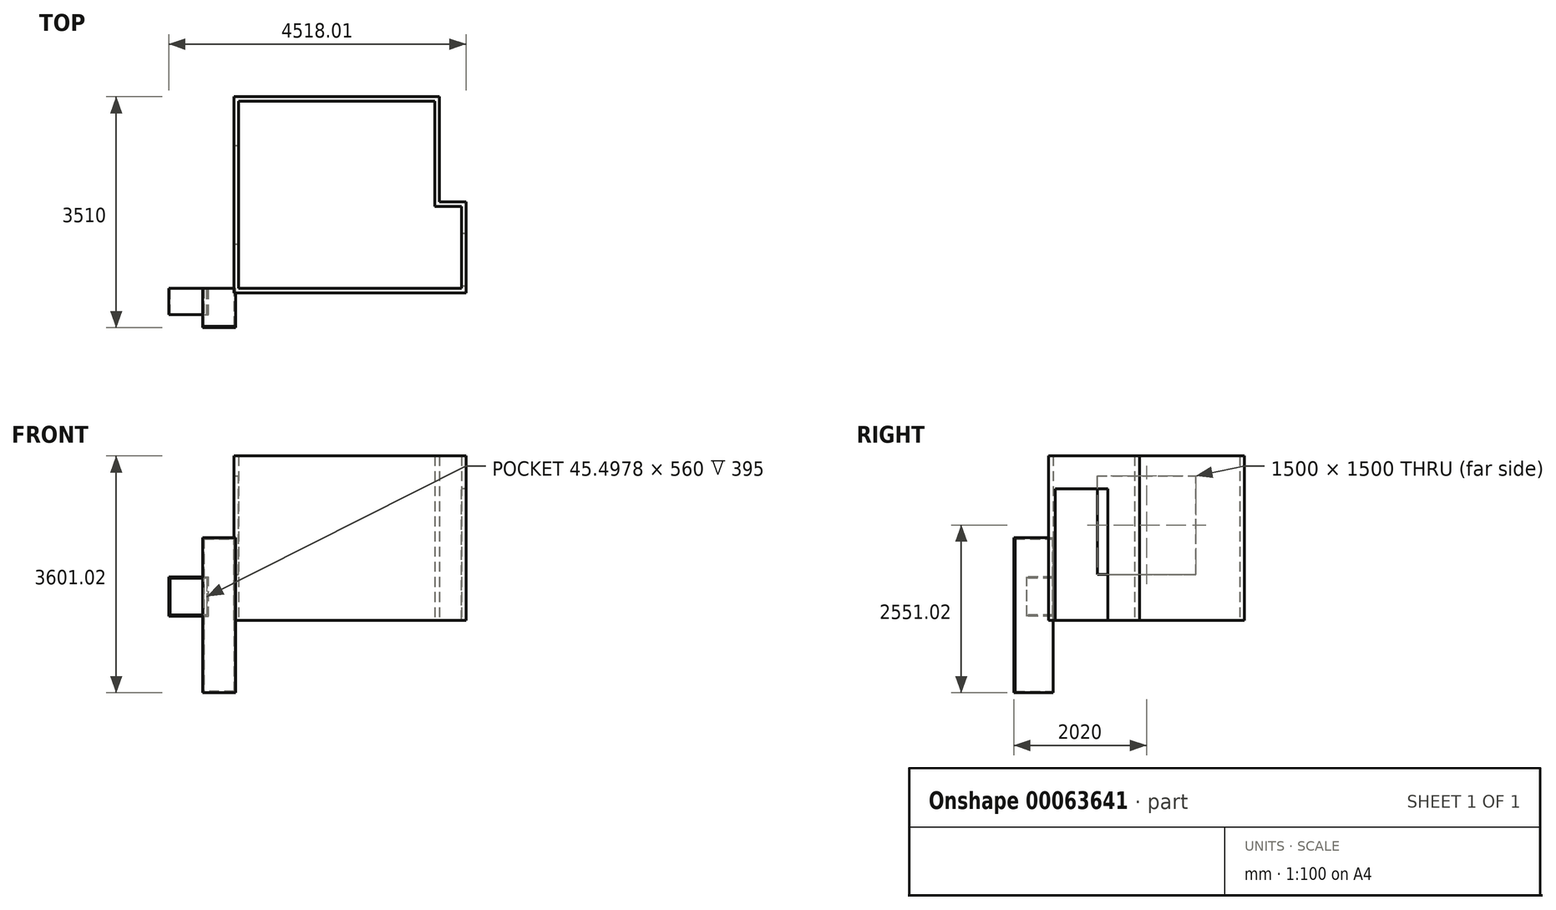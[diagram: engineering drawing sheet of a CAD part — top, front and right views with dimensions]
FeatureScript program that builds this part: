
annotation { "Feature Type Name" : "Feature", "Feature Type Description" : "" }
export const myFeature = defineFeature(function(context is Context, id is Id, definition is map)
    precondition{}
    {
        {
            var Q0;
            Q0=qCreatedBy(makeId("Top.planeOp"),FACE);
            var sketch = newSketch(context, id + "F0", { "sketchPlane" : qUnion([Q0])});
            skLineSegment(sketch, "E0.bottom", {"start": v(0, 0) * mm, "end": v(3390, 0) * mm});
            skLineSegment(sketch, "E0.top", {"start": v(0, 2840) * mm, "end": v(2985, 2840) * mm});
            skLineSegment(sketch, "E0.left", {"start": v(0, 0) * mm, "end": v(0, 2840) * mm});
            skLineSegment(sketch, "E0.right", {"start": v(2985, 1240) * mm, "end": v(2985, 2840) * mm});
            skLineSegment(sketch, "E1", {"start": v(3390, 0) * mm, "end": v(3390, 830) * mm});
            skLineSegment(sketch, "E2", {"start": v(3390, 830) * mm, "end": v(3390, 1240) * mm});
            skLineSegment(sketch, "E3", {"start": v(3390, 1240) * mm, "end": v(2985, 1240) * mm});
            skLineSegment(sketch, "E4.0", {"start": v(3460, 830) * mm, "end": v(3460, 1310) * mm});
            skLineSegment(sketch, "E4.1", {"start": v(3460, -70) * mm, "end": v(3460, 830) * mm});
            skLineSegment(sketch, "E4.2", {"start": v(3055, 1310) * mm, "end": v(3055, 2910) * mm});
            skLineSegment(sketch, "E4.3", {"start": v(-70, 2910) * mm, "end": v(3055, 2910) * mm});
            skLineSegment(sketch, "E4.4", {"start": v(-70, -70) * mm, "end": v(-70, 2910) * mm});
            skLineSegment(sketch, "E4.5", {"start": v(3460, 1310) * mm, "end": v(3055, 1310) * mm});
            skLineSegment(sketch, "E4.6", {"start": v(-70, -70) * mm, "end": v(3460, -70) * mm});
            skSolve(sketch);
        }
        {
            var Q0;
            Q0 = qSketchRegion(id + "F0", true);
            extrude(context, id + "F1", {"entities" : qUnion([Q0]), "depth" : 2500 * mm});
        }
        {
            var Q0;
            Q0=makeQuery(id+"F1.opExtrude","SWEPT_FACE",FACE,{"disambiguationData":[OSD([sQuery(id+"F0.wireOp",EDGE,"E1"),sQuery(id+"F0.wireOp",EDGE,"E2")])]});
            var sketch = newSketch(context, id + "F2", { "sketchPlane" : qUnion([Q0])});
            skLineSegment(sketch, "E5.0", {"start": v(0, 2500) * mm, "end": v(0, 0) * mm, "construction": true});
            skLineSegment(sketch, "E6.bottom", {"start": v(-830, 0) * mm, "end": v(-30, 0) * mm});
            skLineSegment(sketch, "E6.top", {"start": v(-830, 2000) * mm, "end": v(-30, 2000) * mm});
            skLineSegment(sketch, "E6.left", {"start": v(-830, 0) * mm, "end": v(-830, 2000) * mm});
            skLineSegment(sketch, "E6.right", {"start": v(-30, 0) * mm, "end": v(-30, 2000) * mm});
            skSolve(sketch);
        }
        {
            var Q0;
            Q0 = qSketchRegion(id + "F2", true);
            extrude(context, id + "F3", {"entities" : qUnion([Q0]), "operationType" : NewBodyOperationType.REMOVE, "endBound" : BoundingType.UP_TO_NEXT, "oppositeDirection" : true, "depth" : 25 * mm});
        }
        {
            var Q0;
            Q0=makeQuery(id+"F1.opExtrude","SWEPT_FACE",FACE,{"disambiguationData":[OSD([sQuery(id+"F0.wireOp",EDGE,"E0.left")])]});
            var sketch = newSketch(context, id + "F4", { "sketchPlane" : qUnion([Q0])});
            skLineSegment(sketch, "E7.bottom", {"start": v(670, 700) * mm, "end": v(2170, 700) * mm});
            skLineSegment(sketch, "E7.top", {"start": v(670, 2200) * mm, "end": v(2170, 2200) * mm});
            skLineSegment(sketch, "E7.left", {"start": v(670, 700) * mm, "end": v(670, 2200) * mm});
            skLineSegment(sketch, "E7.right", {"start": v(2170, 700) * mm, "end": v(2170, 2200) * mm});
            skSolve(sketch);
        }
        {
            var Q0;
            Q0 = qSketchRegion(id + "F4", true);
            extrude(context, id + "F5", {"entities" : qUnion([Q0]), "operationType" : NewBodyOperationType.REMOVE, "endBound" : BoundingType.UP_TO_NEXT, "oppositeDirection" : true, "depth" : 25 * mm});
        }
        {
            var Q0;
            Q0=qCreatedBy(makeId("Front.planeOp"),FACE);
            var sketch = newSketch(context, id + "F6", { "sketchPlane" : qUnion([Q0])});
            skLineSegment(sketch, "E8.bottom", {"start": v(-543.5, 1258.98) * mm, "end": v(-43.5, 1258.98) * mm});
            skLineSegment(sketch, "E8.top", {"start": v(-543.5, -1101.02) * mm, "end": v(-43.5, -1101.02) * mm});
            skLineSegment(sketch, "E8.left", {"start": v(-543.5, 1258.98) * mm, "end": v(-543.5, -1101.02) * mm});
            skLineSegment(sketch, "E8.right", {"start": v(-43.5, 1258.98) * mm, "end": v(-43.5, -1101.02) * mm});
            skLineSegment(sketch, "E9.0", {"start": v(-523.5, 1238.98) * mm, "end": v(-63.5, 1238.98) * mm});
            skLineSegment(sketch, "E9.1", {"start": v(-523.5, 1238.98) * mm, "end": v(-523.5, -1081.02) * mm});
            skLineSegment(sketch, "E9.2", {"start": v(-523.5, -1081.02) * mm, "end": v(-63.5, -1081.02) * mm});
            skLineSegment(sketch, "E9.3", {"start": v(-63.5, 1238.98) * mm, "end": v(-63.5, -1081.02) * mm});
            skSolve(sketch);
        }
        {
            var Q0;
            Q0 = qSketchRegion(id + "F6", true);
            extrude(context, id + "F7", {"entities" : qUnion([Q0]), "depth" : 580 * mm});
        }
        {
            var Q0;
            Q0=makeQuery(id+"F7.opExtrude","CAP_FACE",FACE,{"disambiguationData":[OSD([sQuery(id+"F6.wireOp",EDGE,"E8.bottom"),sQuery(id+"F6.wireOp",EDGE,"E8.top"),sQuery(id+"F6.wireOp",EDGE,"E8.left"),sQuery(id+"F6.wireOp",EDGE,"E8.right"),sQuery(id+"F6.wireOp",EDGE,"E9.0"),sQuery(id+"F6.wireOp",EDGE,"E9.1"),sQuery(id+"F6.wireOp",EDGE,"E9.2"),sQuery(id+"F6.wireOp",EDGE,"E9.3")])],"isStart":true});
            var sketch = newSketch(context, id + "F8", { "sketchPlane" : qUnion([Q0])});
            skLineSegment(sketch, "E10.bottom", {"start": v(43.5, -1101.02) * mm, "end": v(543.5, -1101.02) * mm});
            skLineSegment(sketch, "E10.top", {"start": v(43.5, 1258.98) * mm, "end": v(543.5, 1258.98) * mm});
            skLineSegment(sketch, "E10.left", {"start": v(43.5, -1101.02) * mm, "end": v(43.5, 1258.98) * mm});
            skLineSegment(sketch, "E10.right", {"start": v(543.5, -1101.02) * mm, "end": v(543.5, 1258.98) * mm});
            skSolve(sketch);
        }
        {
            var Q0;
            Q0 = qSketchRegion(id + "F8", true);
            extrude(context, id + "F9", {"entities" : qUnion([Q0]), "operationType" : NewBodyOperationType.ADD, "oppositeDirection" : true, "depth" : 5 * mm});
        }
        {
            var Q0;
            Q0=makeQuery(id+"F7.opExtrude","CAP_FACE",FACE,{"disambiguationData":[OSD([sQuery(id+"F6.wireOp",EDGE,"E8.bottom"),sQuery(id+"F6.wireOp",EDGE,"E8.top"),sQuery(id+"F6.wireOp",EDGE,"E8.left"),sQuery(id+"F6.wireOp",EDGE,"E8.right"),sQuery(id+"F6.wireOp",EDGE,"E9.0"),sQuery(id+"F6.wireOp",EDGE,"E9.1"),sQuery(id+"F6.wireOp",EDGE,"E9.2"),sQuery(id+"F6.wireOp",EDGE,"E9.3")])],"isStart":false});
            var sketch = newSketch(context, id + "F10", { "sketchPlane" : qUnion([Q0])});
            skLineSegment(sketch, "E11.bottom", {"start": v(-543.5, -1101.02) * mm, "end": v(-43.5, -1101.02) * mm});
            skLineSegment(sketch, "E11.top", {"start": v(-543.5, 1258.98) * mm, "end": v(-43.5, 1258.98) * mm});
            skLineSegment(sketch, "E11.left", {"start": v(-543.5, -1101.02) * mm, "end": v(-543.5, 1258.98) * mm});
            skLineSegment(sketch, "E11.right", {"start": v(-43.5, -1101.02) * mm, "end": v(-43.5, 1258.98) * mm});
            skSolve(sketch);
        }
        {
            var Q0;
            Q0 = qSketchRegion(id + "F10", true);
            extrude(context, id + "F11", {"entities" : qUnion([Q0]), "depth" : 20 * mm});
        }
        {
            var Q0;
            Q0=qCreatedBy(makeId("Front.planeOp"),FACE);
            var sketch = newSketch(context, id + "F12", { "sketchPlane" : qUnion([Q0])});
            skLineSegment(sketch, "E12.bottom", {"start": v(-1058, 61.4) * mm, "end": v(-458, 61.4) * mm});
            skLineSegment(sketch, "E12.top", {"start": v(-1058, 661.4) * mm, "end": v(-458, 661.4) * mm});
            skLineSegment(sketch, "E12.left", {"start": v(-1058, 61.4) * mm, "end": v(-1058, 661.4) * mm});
            skLineSegment(sketch, "E12.right", {"start": v(-458, 61.4) * mm, "end": v(-458, 661.4) * mm});
            skLineSegment(sketch, "E13.0", {"start": v(-478, 81.4) * mm, "end": v(-478, 641.4) * mm});
            skLineSegment(sketch, "E13.1", {"start": v(-1038, 81.4) * mm, "end": v(-478, 81.4) * mm});
            skLineSegment(sketch, "E13.2", {"start": v(-1038, 81.4) * mm, "end": v(-1038, 641.4) * mm});
            skLineSegment(sketch, "E13.3", {"start": v(-1038, 641.4) * mm, "end": v(-478, 641.4) * mm});
            skSolve(sketch);
        }
        {
            var Q0;
            Q0 = qSketchRegion(id + "F12", true);
            extrude(context, id + "F13", {"entities" : qUnion([Q0]), "depth" : 400 * mm});
        }
        {
            var Q0;
            Q0=makeQuery(id+"F13.opExtrude","CAP_FACE",FACE,{"disambiguationData":[OSD([sQuery(id+"F12.wireOp",EDGE,"E12.bottom"),sQuery(id+"F12.wireOp",EDGE,"E12.top"),sQuery(id+"F12.wireOp",EDGE,"E12.left"),sQuery(id+"F12.wireOp",EDGE,"E12.right"),sQuery(id+"F12.wireOp",EDGE,"E13.0"),sQuery(id+"F12.wireOp",EDGE,"E13.1"),sQuery(id+"F12.wireOp",EDGE,"E13.2"),sQuery(id+"F12.wireOp",EDGE,"E13.3")])],"isStart":true});
            var sketch = newSketch(context, id + "F14", { "sketchPlane" : qUnion([Q0])});
            skLineSegment(sketch, "E14.bottom", {"start": v(458, 61.4) * mm, "end": v(1058, 61.4) * mm});
            skLineSegment(sketch, "E14.top", {"start": v(458, 661.4) * mm, "end": v(1058, 661.4) * mm});
            skLineSegment(sketch, "E14.left", {"start": v(458, 61.4) * mm, "end": v(458, 661.4) * mm});
            skLineSegment(sketch, "E14.right", {"start": v(1058, 61.4) * mm, "end": v(1058, 661.4) * mm});
            skSolve(sketch);
        }
        {
            var Q0;
            Q0 = qSketchRegion(id + "F14", true);
            extrude(context, id + "F15", {"entities" : qUnion([Q0]), "operationType" : NewBodyOperationType.ADD, "oppositeDirection" : true, "depth" : 5 * mm});
        }
    });
